# Revit family: Sanitary_Mirrors_hansgrohe_54105CHN-MoonWake-Mirror-800-135_NEW
name_source: partatom
category: Furniture
revit_build: Autodesk Revit 2018 (Build: 20170223_1515(x64)
units: mm (PartAtom-declared; Revit-internal decimal feet)

## family parameters
Always vertical = No
Cut with Voids When Loaded = No
OmniClass Number = 23.40.00.00
OmniClass Title = Equipment and Furnishings
Room Calculation Point = No
Shared = No
Work Plane-Based = Yes

## types (1)
- 467 Basaltgrey
    Always visible = Yes
    BIMobject category = Mirrors
    Default Elevation = 1219.2 mm  [stored 4 ft]
    Description = MoonWake Mirror 800/135
    Design country = Germany
    EAN code = 4059625328774
    Edition number = 1
    GTIN code = https://4059625328774
    IFC Classification = Furnishing Element
    Manufacturer = hansgrohe
    Manufacturer country = Germany
    Manufacturer name = hansgrohe
    Masterformat 2014 Code = 08 83 00
    Masterformat 2014 Description = Mirrors
    Material 1 = Hansgrohe - Wood - 467 Basaltgrey
    Material 2 = Hansgrohe - Glass - Mirror
    Model = 54105CHN
    NBS Reference Code = 45-55-06
    NBS Reference Description = Bathroom Mirrors
    OmniClass Code = 23-21 37 13 15
    OmniClass Description = Mirrors
    Product Guid = 824f8b9e-32d5-4aea-b5ee-b5c8a500be09
    Product SKU = 54105CHN
    Product data url = https://bimobject.com
    Product family = MoonWake
    Product group = Mirrors
    Product name = 54105CHN MoonWake Mirror 800/135
    QR code = https://bimobject.com
    URL = https://www.hansgrohe.com
    Uniclass 2015 Code = Pr_25_71_53_06
    Uniclass 2015 Name = Bathroom mirrors
    Uniformat II Code = E2010
    Uniformat II Description = Fixed Furnishings
    Weight Net (Kg) = 18.5

note: [stored X ft] marks values corroborated as IEEE doubles in the binary element streams (Revit-internal decimal feet)

## geometry (parser evidence)
native form markers: Sweep x4
no freeform markers — native parametric forms only
